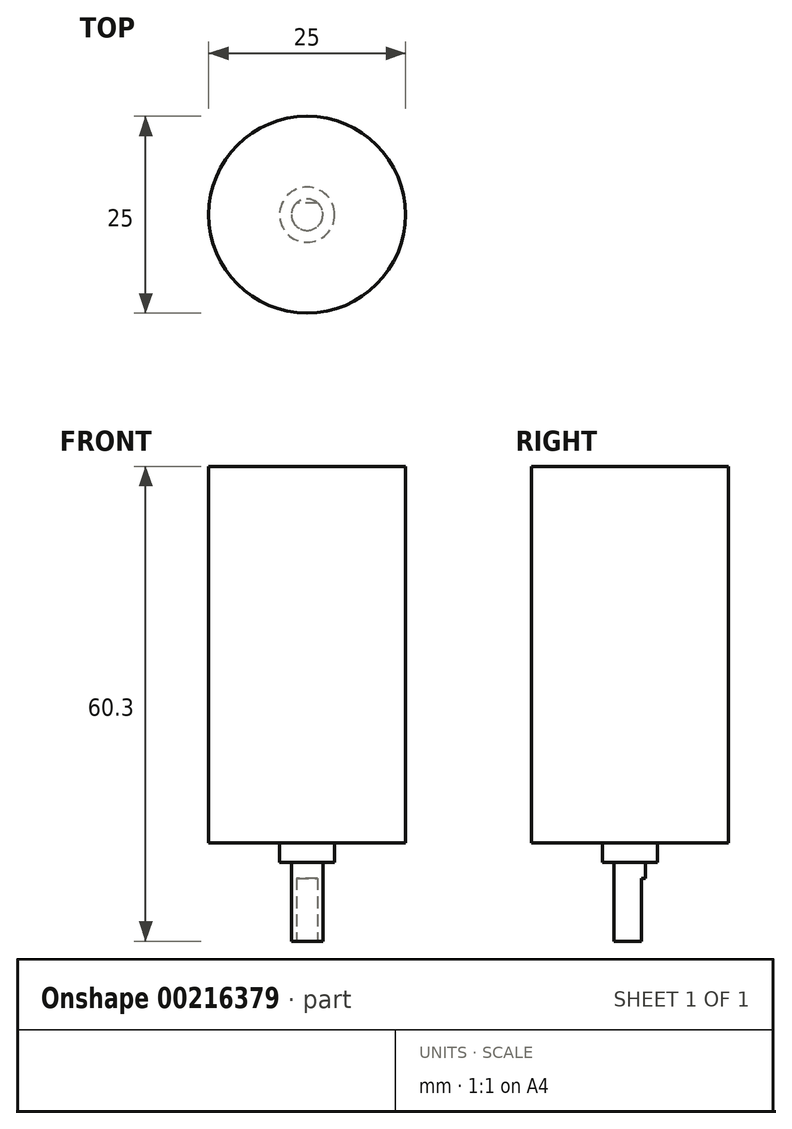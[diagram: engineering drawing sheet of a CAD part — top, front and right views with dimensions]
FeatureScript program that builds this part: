
annotation { "Feature Type Name" : "Feature", "Feature Type Description" : "" }
export const myFeature = defineFeature(function(context is Context, id is Id, definition is map)
    precondition{}
    {
        {
            var Q0;
            Q0=qCreatedBy(makeId("Top.planeOp"),FACE);
            var sketch = newSketch(context, id + "F0", { "sketchPlane" : qUnion([Q0])});
            skCircle(sketch, "E0", {"center": v(0, 0) * mm, "radius": 12.5 * mm});
            skSolve(sketch);
        }
        {
            var Q0;
            Q0=makeQuery(id+"F0.imprint","IMPRINT",FACE,{"disambiguationData":[TD([[makeQuery(id+"F0.imprint","IMPRINT",EDGE,{"derivedFrom":sQuery(id+"F0.wireOp",EDGE,"E0")}),1.0]])]});
            extrude(context, id + "F1", {"entities" : qUnion([Q0]), "depth" : (30.8 + 17) * mm, "offsetDistance" : 25 * mm});
        }
        {
            var Q0;
            Q0=makeQuery(id+"F1.opExtrude","CAP_FACE",FACE,{"disambiguationData":[OSD([sQuery(id+"F0.wireOp",EDGE,"E0")])],"isStart":true});
            var sketch = newSketch(context, id + "F2", { "sketchPlane" : qUnion([Q0])});
            skCircle(sketch, "E1", {"center": v(0, 0) * mm, "radius": 3.5 * mm});
            skSolve(sketch);
        }
        {
            var Q0;
            Q0=makeQuery(id+"F2.imprint","IMPRINT",FACE,{"disambiguationData":[TD([[makeQuery(id+"F2.imprint","IMPRINT",EDGE,{"derivedFrom":sQuery(id+"F2.wireOp",EDGE,"E1")}),1.0]])]});
            extrude(context, id + "F3", {"entities" : qUnion([Q0]), "operationType" : NewBodyOperationType.ADD, "depth" : 2.5 * mm, "offsetDistance" : 25 * mm});
        }
        {
            var Q0;
            Q0=makeQuery(id+"F1.opExtrude","CAP_FACE",FACE,{"disambiguationData":[OSD([sQuery(id+"F0.wireOp",EDGE,"E0")])],"isStart":true});
            var sketch = newSketch(context, id + "F4", { "sketchPlane" : qUnion([Q0])});
            skCircle(sketch, "E2", {"center": v(0, 0) * mm, "radius": 2 * mm});
            skSolve(sketch);
        }
        {
            var Q0;
            Q0 = qSketchRegion(id + "F4", true);
            extrude(context, id + "F5", {"entities" : qUnion([Q0]), "operationType" : NewBodyOperationType.ADD, "depth" : 12.5 * mm, "offsetDistance" : 25 * mm});
        }
        {
            var Q0;
            Q0=makeQuery(id+"F5.opExtrude","CAP_FACE",FACE,{"disambiguationData":[OSD([sQuery(id+"F4.wireOp",EDGE,"E2")])],"isStart":false});
            var sketch = newSketch(context, id + "F6", { "sketchPlane" : qUnion([Q0])});
            skLineSegment(sketch, "E3", {"start": v(1.32, -1.5) * mm, "end": v(-1.32, -1.5) * mm});
            skArc(sketch, "E4", {"start": v(1.32, -1.5) * mm, "mid": v(0, -2) * mm, "end": v(-1.32, -1.5) * mm});
            skSolve(sketch);
        }
        {
            var Q0;
            Q0 = qSketchRegion(id + "F6", true);
            extrude(context, id + "F7", {"entities" : qUnion([Q0]), "operationType" : NewBodyOperationType.REMOVE, "oppositeDirection" : true, "depth" : 8 * mm, "offsetDistance" : 25 * mm});
        }
    });
